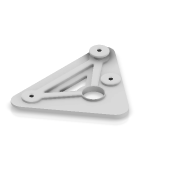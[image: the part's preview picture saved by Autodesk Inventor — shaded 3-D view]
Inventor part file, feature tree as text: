
AUTODESK INVENTOR PART (.ipt)
format: ipt  version: 2022 (Build 260153000, 153)  size: 352,256 bytes
history: native  units: mm
features: extrude x9, sketch x8, hole x7, fillet x3, plane x2, other x2, split x1
ambient origin geometry x8: Origin, YZ Plane, XZ Plane, XY Plane, X Axis, Y Axis, Z Axis, Center Point
bodies: Body1 (feature_tree), Body2 (feature_tree)
feature tree (32):
  sketch  "Boceto1"  dims[d2=18.0mm d4=10.0mm]
  extrude  "Extrusión6"  Depth=10.0mm
  hole  "Agujero1"  [1 undecoded]
  hole  "Agujero2"  [1 undecoded]
  hole  "Agujero6"  [1 undecoded]
  plane  "Plano de trabajo5"
  extrude  "Extrusión11"  Depth=1.0mm TaperAngle=0.0deg
  extrude  "Extrusión12"  Depth=1.0mm TaperAngle=0.0deg
  extrude  "Extrusión15"  Depth=1.0mm TaperAngle=0.0deg
  extrude  "Extrusión16"  Depth=10.0mm
  hole  "Agujero9"  [1 undecoded]
  hole  "Agujero10"  [1 undecoded]
  extrude  "Extrusión17"  Depth=1.0mm TaperAngle=0.0deg
  extrude  "Extrusión18"  Depth=1.0mm
  extrude  "Extrusión19"  Depth=1.0mm
  extrude  "Extrusión20"  Depth=1.0mm
  fillet  "Empalme6"  [1 undecoded]
  fillet  "Empalme7"  [1 undecoded]
  fillet  "Empalme8"  [1 undecoded]
  sketch  "Boceto16"  dims[d152=20.0mm d154=20.0mm]
  plane  "Plano de trabajo6"
  hole  "Agujero11"  [1 undecoded]
  hole  "Agujero13"  [1 undecoded]
  split  "Dividir4"
  sketch  "Boceto6"  dims[d62=6.0mm d63=0.0mm]
  sketch  "Boceto13"  dims[d72=3.5mm d82=9.0mm d83=6.0mm d84=4.0mm d85=2.0mm d86=90.0deg d87=3.0mm d88=0.0mm]
  sketch  "Boceto14"  dims[d89=9.0mm d90=6.0mm d91=4.0mm d92=2.0mm d93=90.0deg d94=4.5mm d95=0.0mm]
  sketch  "Boceto15"  dims[d117=4.0mm d118=6.0mm d119=7.0mm d120=2.0mm d121=90.0deg d122=8.0mm d123=20.594885mm d147=42.0mm]
  sketch  "Boceto18"  dims[d155=0.0mm d156=0.0mm d157=13.009mm d158=0.0mm]
  other  "Sup2"
  sketch  "Boceto20"  dims[d164=6.0mm d165=0.0mm d166=6.0mm d167=0.0mm d168=9.0mm d169=6.0mm d170=4.0mm d171=2.0mm d172=90.0deg d173=4.5mm d174=0.0mm d175=4.0mm d176=6.0mm d177=7.0mm d178=2.0mm d179=90.0deg d180=8.0mm d181=0.0mm d193=3.0mm d194=0.0mm d195=4.0mm d196=0.0mm d197=10.0mm d198=5.0mm d199=0.0mm d200=18.0mm d201=2.0mm d202=0.0mm d203=0.5mm d204=0.5mm d205=1.0mm d206=-94.0mm d207=0.0mm d208=90.0deg d209=0.0mm d210=90.0deg d211=9.0mm d212=6.0mm d213=4.0mm d214=2.0mm d215=90.0deg d216=11.5mm d217=0.0mm d225=4.0mm d226=6.0mm d227=7.0mm d228=2.0mm d229=90.0deg d230=10.4mm d231=0.0mm d233=10.0mm d235=84.0mm d236=34.718979mm d237=12.0mm d17=0.5mm d18=0.872665mm d19=0.5mm d20=0.872665mm d26=0.5mm d27=0.872665mm d28=0.5mm d29=0.872665mm d103=1.0mm d104=1.0mm d105=1.0mm d106=0.15mm d107=0.25mm d108=0.375mm d109=14.3117mm d110=0.75mm d111=20.594885mm d112=0.0625mm d113=0.75mm d114=0.375mm d159=0.5mm d160=0.872665mm d161=0.5mm d162=0.872665mm d182=0.75mm d183=20.594885mm d184=0.0625mm d185=0.75mm d186=0.375mm d232=1.0mm d234=1.0mm d238=14.3117mm d239=0.75mm d240=20.594885mm d241=0.0625mm d242=0.75mm d243=0.375mm]
  other  "SuperficieSolevación2"
note: 10 required parameter values undecoded (feature->parameter linkage not recoverable at this tier; creation-order binding heuristic only, values carry confidence <= 0.55)
